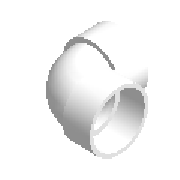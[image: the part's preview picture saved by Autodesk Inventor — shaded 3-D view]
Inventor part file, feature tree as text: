
AUTODESK INVENTOR PART (.ipt)
format: ipt  version: 2023.1 (Build 271208000, 208)  size: 242,176 bytes
history: native  units: mm (DEFAULTED — no unit token found)
features: other x6, sketch x4
ambient origin geometry x8: Origin, YZ Plane, XZ Plane, XY Plane, X Axis, Y Axis, Z Axis, Center Point
bodies: Solid1 (feature_tree)
feature tree (10):
  other  "Work Point1"
  other  "Work Point2"
  other  "Work Axis1"
  other  "Work Point3"
  other  "Work Axis2"
  other  "Work Point4"
  sketch  "Sketch1"  dims[d1=76.4mm]
  sketch  "Sketch2"  dims[d2=75.7mm]
  sketch  "Sketch3"  dims[d0=76.4mm]
  sketch  "Sketch4"  dims[d3=75.7mm d4=3.0mm d5=35.0mm d6=3.0mm d7=67.0mm d39=90.0deg d8=67.0mm d9=3.1mm d10=39.0mm d11=39.0mm d12=39.0mm d13=0.0mm d14=3.1mm d15=35.0mm d16=3.0mm d17=76.4mm d18=75.7mm d19=67.0mm d82=90.0deg d83=0.0mm]
